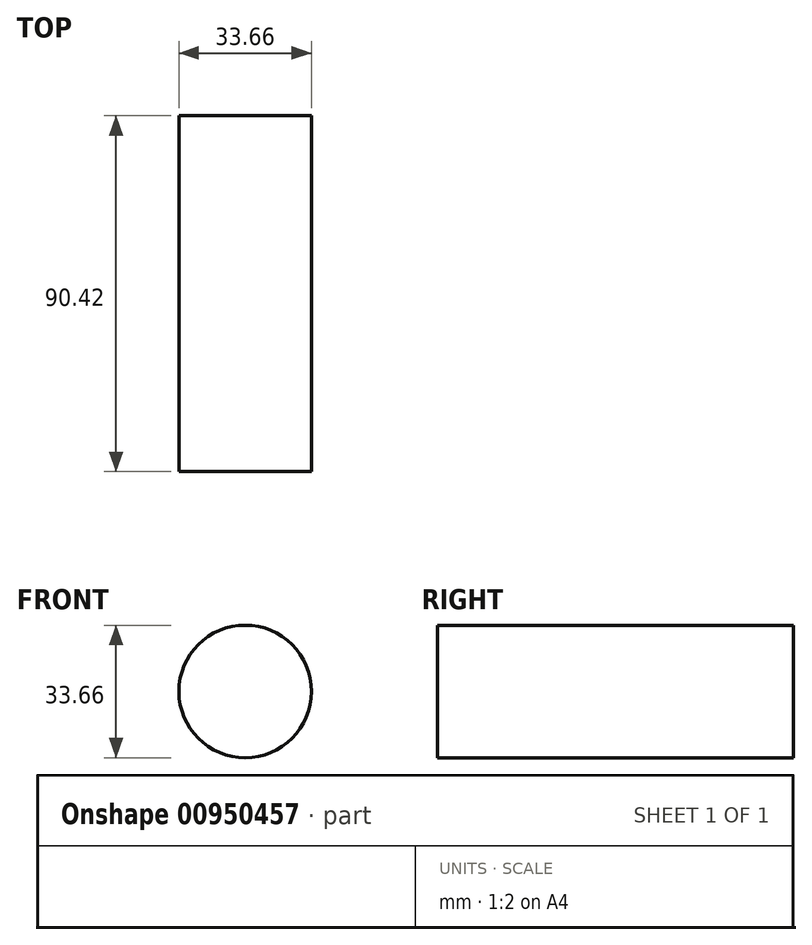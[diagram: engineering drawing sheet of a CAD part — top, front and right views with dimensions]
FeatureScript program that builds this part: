
annotation { "Feature Type Name" : "Feature", "Feature Type Description" : "" }
export const myFeature = defineFeature(function(context is Context, id is Id, definition is map)
    precondition{}
    {
        {
            var Q0;
            Q0=qCreatedBy(makeId("Front.planeOp"),FACE);
            var sketch = newSketch(context, id + "F0", { "sketchPlane" : qUnion([Q0])});
            skCircle(sketch, "E0", {"center": v(0, 0) * mm, "radius": 16.83 * mm});
            skSolve(sketch);
        }
        {
            var Q0;
            Q0=makeQuery(id+"F0.imprint","IMPRINT",FACE,{"disambiguationData":[TD([[makeQuery(id+"F0.imprint","IMPRINT",EDGE,{"derivedFrom":sQuery(id+"F0.wireOp",EDGE,"E0")}),1.0]])]});
            extrude(context, id + "F1", {"entities" : qUnion([Q0]), "depth" : 90.42 * mm, "offsetDistance" : 25.4 * mm});
        }
    });
